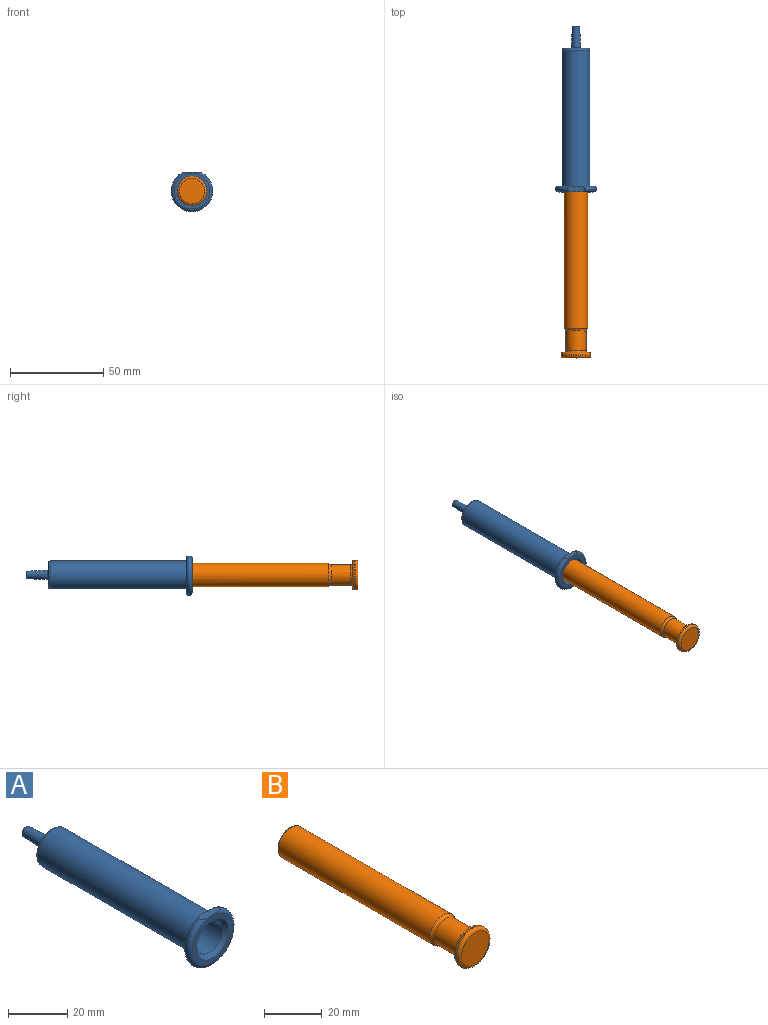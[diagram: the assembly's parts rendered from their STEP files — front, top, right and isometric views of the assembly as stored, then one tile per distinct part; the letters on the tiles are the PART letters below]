
ASSEMBLY  parts=2 mates=1
PART A: 16 faces, bbox 24.1x89x24.1 mm
  f0: cylinder r=6.25mm len=74mm, axis (0,1,0), area 2906mm2, adj f7,f8
  f1: cylinder r=7.5mm len=73mm, axis (0,1,0), area 3440mm2, adj f4,f9
  f2: plane 19.25x19.25mm, normal (0,-1,0), area 102.3mm2, adj f5,f7
  f3: plane 13x13mm, normal (0,1,0), area 104.8mm2, adj f9,f13
  f4: plane 19.25x19.25mm, normal (0,1,0), area 114.3mm2, adj f1,f5
  f5: torus R=9.62mm, axis (0,-1,0), area 283mm2, adj f2,f4,f6
  f6: plane 9.75x2.91mm, normal (0,0,1), area 23.7mm2, adj f5
  f7: cone r=6.25mm half-angle=45deg, axis (0,-1,0), area 93.3mm2, adj f0,f2
  f8: plane 12.5x12.5mm, normal (0,-1,0), area 103.1mm2, adj f0,f15
  f9: torus R=6.5mm, axis (0,-1,0), area 70.4mm2, adj f1,f3
  f10: plane 4x4mm, normal (0,1,0), area 5.5mm2, adj f11,f12
  f11: cone r=1.5mm half-angle=2.4deg, axis (0,-1,0), area 132.1mm2, adj f10,f14
  f12: cone r=2.5mm half-angle=2.4deg, axis (0,-1,0), area 162.3mm2, adj f10,f13
  f13: torus R=2.98mm, axis (0,-1,0), area 12.8mm2, adj f3,f12
  f14: cylinder r=2mm len=4mm, axis (0,1,0), area 12.6mm2, adj f11,f15
  f15: torus R=2.5mm, axis (0,1,0), area 10.8mm2, adj f8,f14
PART B: 16 faces, bbox 17.3x91x17.3 mm
  f0: cylinder r=6.22mm len=74.5mm, axis (0,1,0), area 2913.9mm2, adj f3,f4
  f1: plane 11.45x11.45mm, normal (0,1,0), area 103mm2, adj f4
  f2: cylinder r=5.5mm len=11mm, axis (0,-1,0), area 370.1mm2, adj f3,f10
  f3: torus R=7.5mm, axis (0,1,0), area 63.5mm2, adj f0,f2
  f4: torus R=5.72mm, axis (0,-1,0), area 29.8mm2, adj f0,f1
  f5: plane 13.5x13.5mm, normal (0,1,0), area 20.4mm2, adj f8,f10
  f6: plane 13.5x13.5mm, normal (0,-1,0), area 143.1mm2, adj f9
  f7: cylinder r=8mm len=16mm, axis (0,1,0), area 25.1mm2, adj f8,f9
  f8: torus R=6.75mm, axis (0,-1,0), area 93.1mm2, adj f5,f7
  f9: torus R=6.75mm, axis (0,-1,0), area 93.1mm2, adj f6,f7
  f10: torus R=6.25mm, axis (0,-1,0), area 42.7mm2, adj f2,f5
  f11: plane 10.95x10.95mm, normal (0,-1,0), area 94.2mm2, adj f12
  f12: cylinder r=5.47mm len=73.93mm, axis (0,1,0), area 2543.2mm2, adj f11,f13
  f13: torus R=7.5mm, axis (0,1,0), area 64.2mm2, adj f12,f14
  f14: cylinder r=4.75mm len=11.46mm, axis (0,-1,0), area 342mm2, adj f13,f15
  f15: plane 9.5x9.5mm, normal (0,1,0), area 70.9mm2, adj f14
PLACE A t=(0.03,-11.95,0.22)mm fixed
PLACE B rot(axis=(0,-1,0),0deg) t=(0.03,-86.95,0.22)mm
MATE slider B.f0 <-> A.f0  axis (0,1,0) through (0.03,-87.45,0.22)mm
